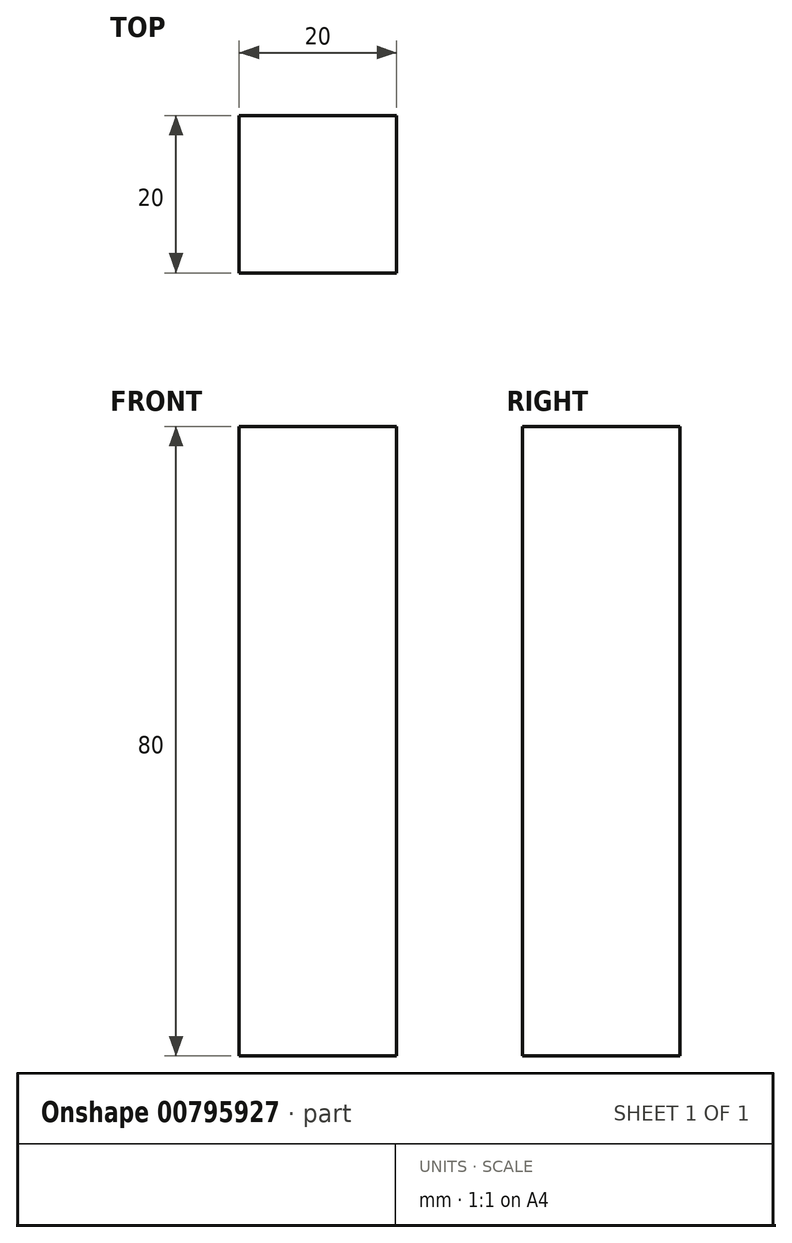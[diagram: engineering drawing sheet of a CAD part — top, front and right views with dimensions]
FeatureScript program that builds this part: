
annotation { "Feature Type Name" : "Feature", "Feature Type Description" : "" }
export const myFeature = defineFeature(function(context is Context, id is Id, definition is map)
    precondition{}
    {
        {
            var Q0;
            Q0=qCreatedBy(makeId("Top.planeOp"),FACE);
            var sketch = newSketch(context, id + "F0", { "sketchPlane" : qUnion([Q0])});
            skLineSegment(sketch, "E0.bottom", {"start": v(10, -10) * mm, "end": v(-10, -10) * mm});
            skLineSegment(sketch, "E0.top", {"start": v(10, 10) * mm, "end": v(-10, 10) * mm});
            skLineSegment(sketch, "E0.left", {"start": v(10, -10) * mm, "end": v(10, 10) * mm});
            skLineSegment(sketch, "E0.right", {"start": v(-10, -10) * mm, "end": v(-10, 10) * mm});
            skPoint(sketch, "E0.middle", {"position": v(0, 0) * mm});
            skSolve(sketch);
        }
        {
            var Q0;
            Q0=makeQuery(id+"F0.imprint","IMPRINT",FACE,{"disambiguationData":[TD([[makeQuery(id+"F0.imprint","IMPRINT",EDGE,{"derivedFrom":sQuery(id+"F0.wireOp",EDGE,"E0.bottom")}),-1.0]])]});
            extrude(context, id + "F1", {"entities" : qUnion([Q0]), "depth" : 80 * mm, "offsetDistance" : 25 * mm});
        }
    });
